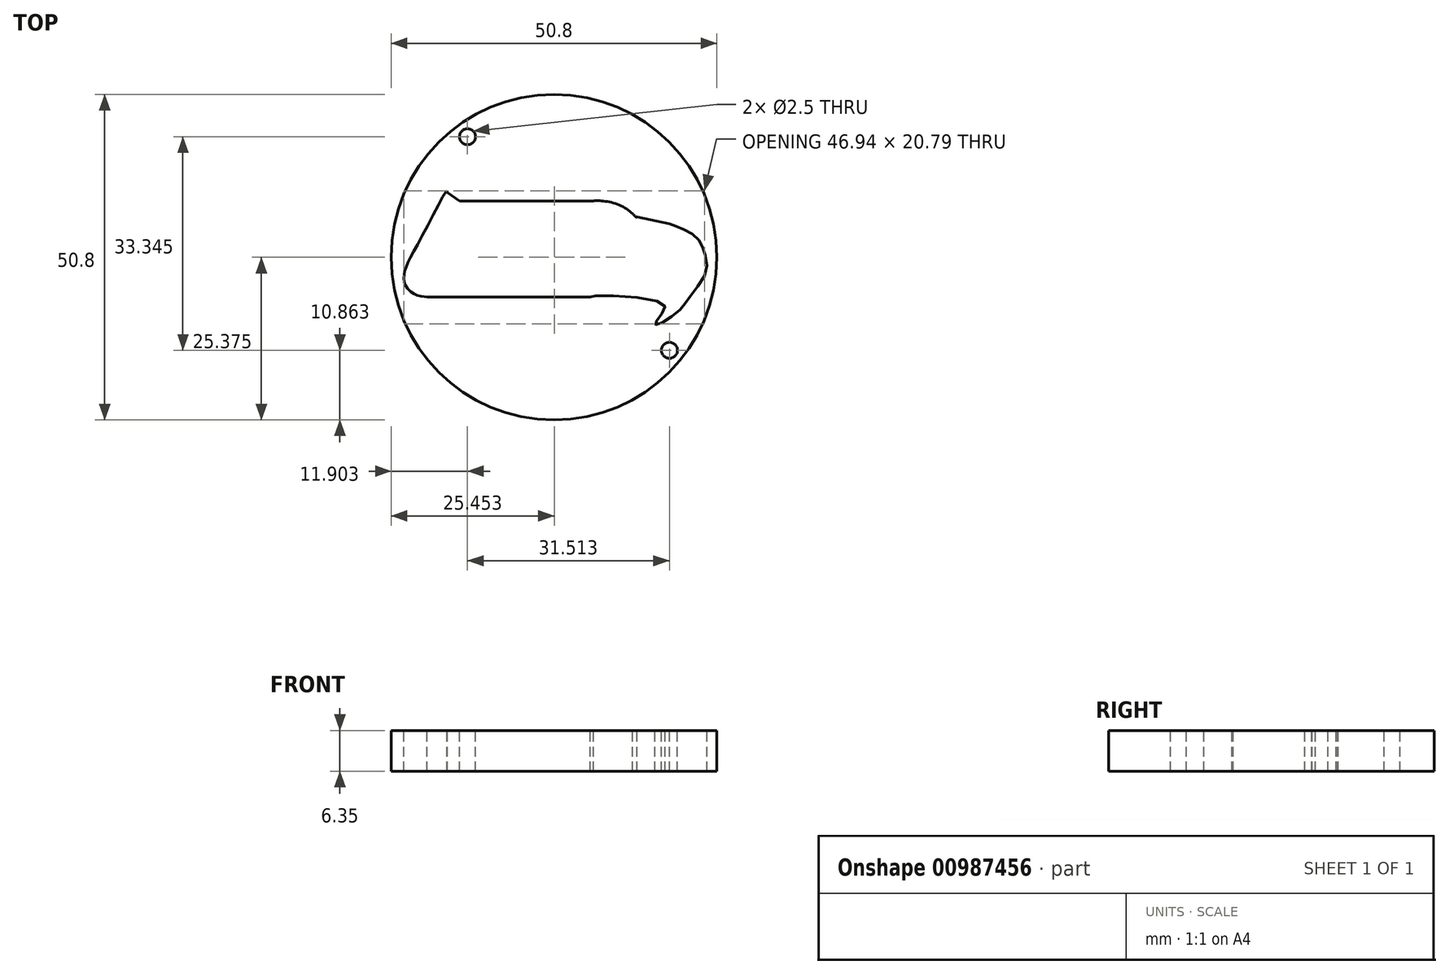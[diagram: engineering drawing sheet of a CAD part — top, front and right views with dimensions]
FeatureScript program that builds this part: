
annotation { "Feature Type Name" : "Feature", "Feature Type Description" : "" }
export const myFeature = defineFeature(function(context is Context, id is Id, definition is map)
    precondition{}
    {
        {
            var Q0;
            Q0=qCreatedBy(makeId("Top.planeOp"),FACE);
            var sketch = newSketch(context, id + "F0", { "sketchPlane" : qUnion([Q0])});
            skCircle(sketch, "E0", {"center": v(0, 0) * mm, "radius": 25.4 * mm});
            skCircle(sketch, "E1", {"center": v(-13.5, 18.8) * mm, "radius": 1.25 * mm});
            skCircle(sketch, "E2", {"center": v(18.02, -14.54) * mm, "radius": 1.25 * mm});
            skSolve(sketch);
        }
        {
            var Q0;
            Q0 = qSketchRegion(id + "F0", true);
            extrude(context, id + "F1", {"entities" : qUnion([Q0]), "oppositeDirection" : true, "depth" : 6.35 * mm, "offsetDistance" : 25 * mm});
        }
        {
            var Q0;
            Q0=makeQuery(id+"F1.opExtrude","CAP_FACE",FACE,{"disambiguationData":[OSD([sQuery(id+"F0.wireOp",EDGE,"E0"),sQuery(id+"F0.wireOp",EDGE,"E1"),sQuery(id+"F0.wireOp",EDGE,"E2")])],"isStart":true});
            var sketch = newSketch(context, id + "F2", { "sketchPlane" : qUnion([Q0])});
            skLineSegment(sketch, "E3", {"start": v(-14.7, 8.79) * mm, "end": v(6.18, 8.79) * mm});
            skFitSpline(sketch, "E4", {"points": [v(6.18, 8.79) * mm, v(7.3, 8.79) * mm, v(10.06, 8.2) * mm, v(12.25, 6.83) * mm], "startDerivative": vector(3.98, 0.2) * mm, "endDerivative": vector(5.38, -4.2) * mm});
            skFitSpline(sketch, "E5", {"points": [v(12.25, 6.83) * mm, v(12.87, 6.25) * mm, v(12.94, 6.33) * mm, v(12.94, 6.3) * mm], "startDerivative": vector(1.17, -1.46) * mm, "endDerivative": vector(-0.05, -0.44) * mm});
            skLineSegment(sketch, "E6", {"start": v(12.94, 6.3) * mm, "end": v(18.05, 5.21) * mm});
            skFitSpline(sketch, "E7", {"points": [v(18.05, 5.21) * mm, v(19.7, 4.56) * mm, v(22.32, 3.02) * mm, v(23.4, 0.99) * mm, v(23.73, -2.28) * mm, v(21, -6.39) * mm, v(19.59, -8.3) * mm, v(16.32, -10.44) * mm, v(15.75, -10.44) * mm, v(16.86, -8.77) * mm, v(16.98, -7.23) * mm, v(5.8, -6.08) * mm, v(5.64, -6.2) * mm], "startDerivative": vector(21.81, -8.16) * mm, "endDerivative": vector(-1.19, -5.49) * mm});
            skLineSegment(sketch, "E8", {"start": v(5.64, -6.2) * mm, "end": v(-19.8, -6.2) * mm});
            skFitSpline(sketch, "E9", {"points": [v(-19.8, -6.2) * mm, v(-20.82, -6.06) * mm, v(-22.12, -5.57) * mm, v(-23.23, -4.3) * mm, v(-23.41, -3.02) * mm, v(-23.05, -1.4) * mm, v(-20.9, 2.73) * mm, v(-16.77, 10.37) * mm, v(-16.73, 10.37) * mm], "startDerivative": vector(-10.92, 1.06) * mm, "endDerivative": vector(1.66, -1.1) * mm});
            skLineSegment(sketch, "E10", {"start": v(-16.73, 10.37) * mm, "end": v(-16.64, 10.1) * mm});
            skFitSpline(sketch, "E11", {"points": [v(-16.64, 10.1) * mm, v(-14.7, 8.79) * mm], "startDerivative": vector(1.93, -1.3) * mm, "endDerivative": vector(1.93, -1.3) * mm});
            skSolve(sketch);
        }
        {
            var Q0;
            Q0=makeQuery(id+"F2.imprint","IMPRINT",FACE,{"disambiguationData":[TD([[makeQuery(id+"F2.imprint","IMPRINT",EDGE,{"derivedFrom":sQuery(id+"F2.wireOp",EDGE,"E3")}),-1.0]])]});
            extrude(context, id + "F3", {"entities" : qUnion([Q0]), "operationType" : NewBodyOperationType.REMOVE, "endBound" : BoundingType.THROUGH_ALL, "oppositeDirection" : true, "depth" : 25 * mm, "offsetDistance" : 25 * mm});
        }
    });
